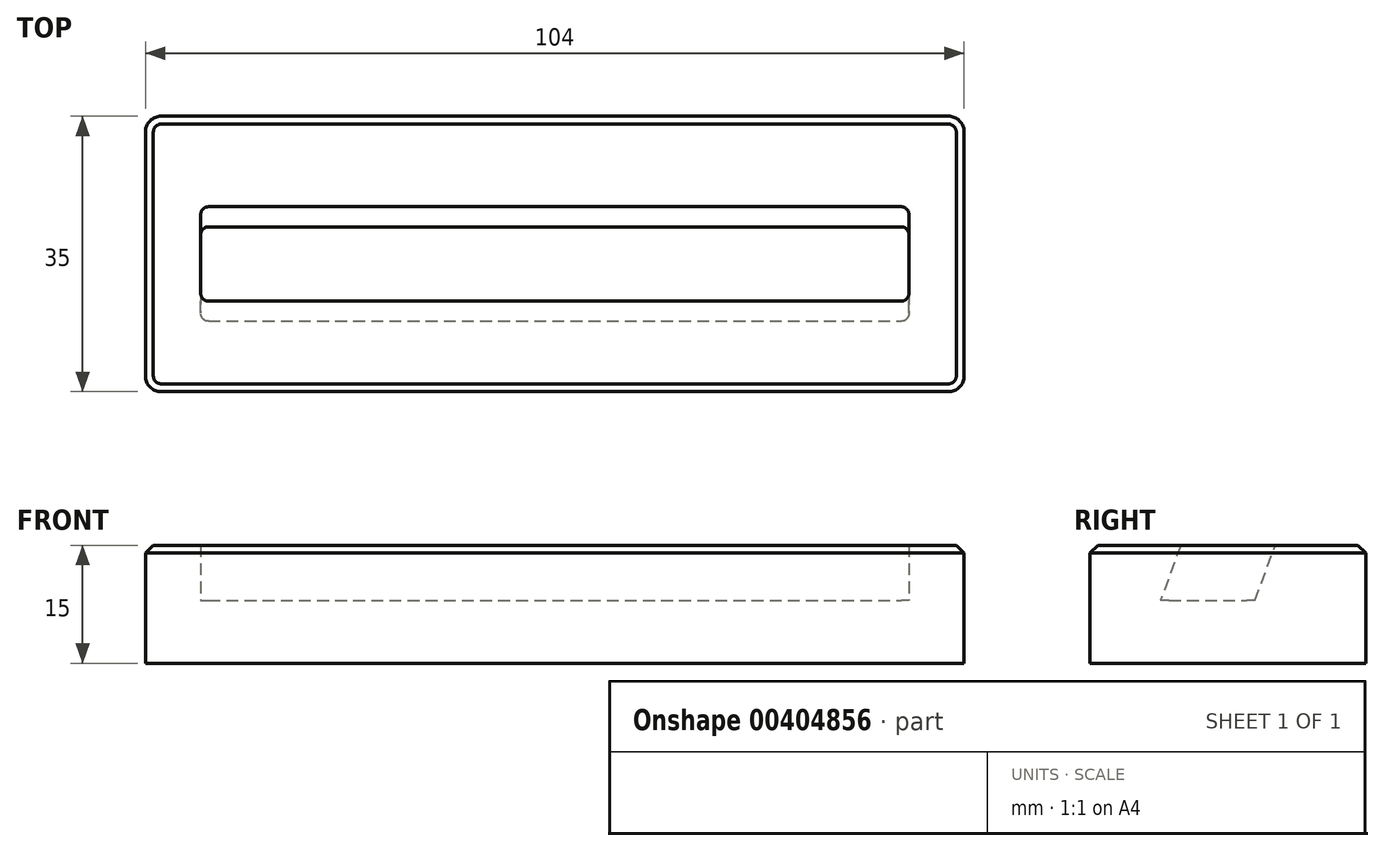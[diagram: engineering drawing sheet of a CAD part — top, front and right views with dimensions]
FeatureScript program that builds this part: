
annotation { "Feature Type Name" : "Feature", "Feature Type Description" : "" }
export const myFeature = defineFeature(function(context is Context, id is Id, definition is map)
    precondition{}
    {
        {
            var Q0;
            Q0=qCreatedBy(makeId("Top.planeOp"),FACE);
            var sketch = newSketch(context, id + "F0", { "sketchPlane" : qUnion([Q0])});
            skLineSegment(sketch, "E0.bottom", {"start": v(0, 0) * mm, "end": v(104, 0) * mm});
            skLineSegment(sketch, "E0.top", {"start": v(0, 35) * mm, "end": v(104, 35) * mm});
            skLineSegment(sketch, "E0.left", {"start": v(0, 0) * mm, "end": v(0, 35) * mm});
            skLineSegment(sketch, "E0.right", {"start": v(104, 0) * mm, "end": v(104, 35) * mm});
            skSolve(sketch);
        }
        {
            var Q0;
            Q0=makeQuery(id+"F0.imprint","IMPRINT",FACE,{"disambiguationData":[TD([[makeQuery(id+"F0.imprint","IMPRINT",EDGE,{"derivedFrom":sQuery(id+"F0.wireOp",EDGE,"E0.bottom")}),1.0]])]});
            extrude(context, id + "F1", {"entities" : qUnion([Q0]), "depth" : 15 * mm});
        }
        {
            var Q0;
            Q0=makeQuery(id+"F1.opExtrude","SWEPT_FACE",FACE,{"disambiguationData":[OSD([sQuery(id+"F0.wireOp",EDGE,"E0.right")])]});
            cPlane(context, id + "F2", {"entities" : qUnion([Q0]), "cplaneType" : CPlaneType.OFFSET, "offset" : 7 * mm, "oppositeDirection" : true, "width" : 150 * mm, "height" : 150 * mm});
        }
        {
            var Q0;
            Q0=qCreatedBy(id+"F2.planeOp",FACE);
            var sketch = newSketch(context, id + "F3", { "sketchPlane" : qUnion([Q0])});
            skLineSegment(sketch, "E1", {"start": v(11.5, 15) * mm, "end": v(8.95, 8) * mm});
            skLineSegment(sketch, "E2", {"start": v(8.95, 8) * mm, "end": v(20.95, 8) * mm});
            skLineSegment(sketch, "E3", {"start": v(20.95, 8) * mm, "end": v(23.5, 15) * mm});
            skLineSegment(sketch, "E4", {"start": v(23.5, 15) * mm, "end": v(11.5, 15) * mm});
            skLineSegment(sketch, "E5", {"start": v(17.5, 15) * mm, "end": v(17.5, 0) * mm, "construction": true});
            skSolve(sketch);
        }
        {
            var Q0;
            Q0 = qSketchRegion(id + "F3", true);
            extrude(context, id + "F4", {"entities" : qUnion([Q0]), "operationType" : NewBodyOperationType.REMOVE, "oppositeDirection" : true, "depth" : 90 * mm});
        }
        {
            var Q0;
            Q0=makeQuery(id+"F4.boolean.opBoolean","COPY",EDGE,{"derivedFrom":makeQuery(id+"F4.opExtrude","CAP_EDGE",EDGE,{"disambiguationData":[OSD([sQuery(id+"F3.wireOp",EDGE,"E3")])],"isStart":false})});
            var Q1;
            Q1=makeQuery(id+"F4.boolean.opBoolean","COPY",EDGE,{"derivedFrom":makeQuery(id+"F4.opExtrude","CAP_EDGE",EDGE,{"disambiguationData":[OSD([sQuery(id+"F3.wireOp",EDGE,"E1")])],"isStart":false})});
            var Q2;
            Q2=makeQuery(id+"F4.boolean.opBoolean","COPY",EDGE,{"derivedFrom":makeQuery(id+"F4.opExtrude","CAP_EDGE",EDGE,{"disambiguationData":[OSD([sQuery(id+"F3.wireOp",EDGE,"E3")])],"isStart":true})});
            var Q3;
            Q3=makeQuery(id+"F4.boolean.opBoolean","COPY",EDGE,{"derivedFrom":makeQuery(id+"F4.opExtrude","CAP_EDGE",EDGE,{"disambiguationData":[OSD([sQuery(id+"F3.wireOp",EDGE,"E1")])],"isStart":true})});
            fillet(context, id + "F5", {"entities" : qUnion([Q0, Q1, Q2, Q3]), "radius" : 1 * mm, "tangentPropagation" : true, "allowEdgeOverflow" : false});
        }
        {
            var Q0;
            Q0=makeQuery(id+"F1.opExtrude","SWEPT_EDGE",EDGE,{"disambiguationData":[OSD([sQuery(id+"F0.wireOp",EDGE,"E0.bottom"),sQuery(id+"F0.wireOp",EDGE,"E0.left")])]});
            var Q1;
            Q1=makeQuery(id+"F1.opExtrude","SWEPT_EDGE",EDGE,{"disambiguationData":[OSD([sQuery(id+"F0.wireOp",EDGE,"E0.bottom"),sQuery(id+"F0.wireOp",EDGE,"E0.right")])]});
            var Q2;
            Q2=makeQuery(id+"F1.opExtrude","SWEPT_EDGE",EDGE,{"disambiguationData":[OSD([sQuery(id+"F0.wireOp",EDGE,"E0.top"),sQuery(id+"F0.wireOp",EDGE,"E0.right")])]});
            var Q3;
            Q3=makeQuery(id+"F1.opExtrude","SWEPT_EDGE",EDGE,{"disambiguationData":[OSD([sQuery(id+"F0.wireOp",EDGE,"E0.top"),sQuery(id+"F0.wireOp",EDGE,"E0.left")])]});
            fillet(context, id + "F6", {"entities" : qUnion([Q0, Q1, Q2, Q3]), "radius" : 2 * mm, "tangentPropagation" : true, "allowEdgeOverflow" : false});
        }
        {
            var Q0;
            Q0=makeQuery(id+"F1.opExtrude","CAP_EDGE",EDGE,{"disambiguationData":[OSD([sQuery(id+"F0.wireOp",EDGE,"E0.top")])],"isStart":false});
            var Q1;
            Q1=makeQuery(id+"F4.boolean.opBoolean","COPY",EDGE,{"derivedFrom":makeQuery(id+"F4.opExtrude","CAP_EDGE",EDGE,{"disambiguationData":[OSD([sQuery(id+"F3.wireOp",EDGE,"E4")])],"isStart":true})});
            chamfer(context, id + "F7", {"entities" : qUnion([Q0, Q1]), "width" : 1 * mm, "tangentPropagation" : true});
        }
    });
